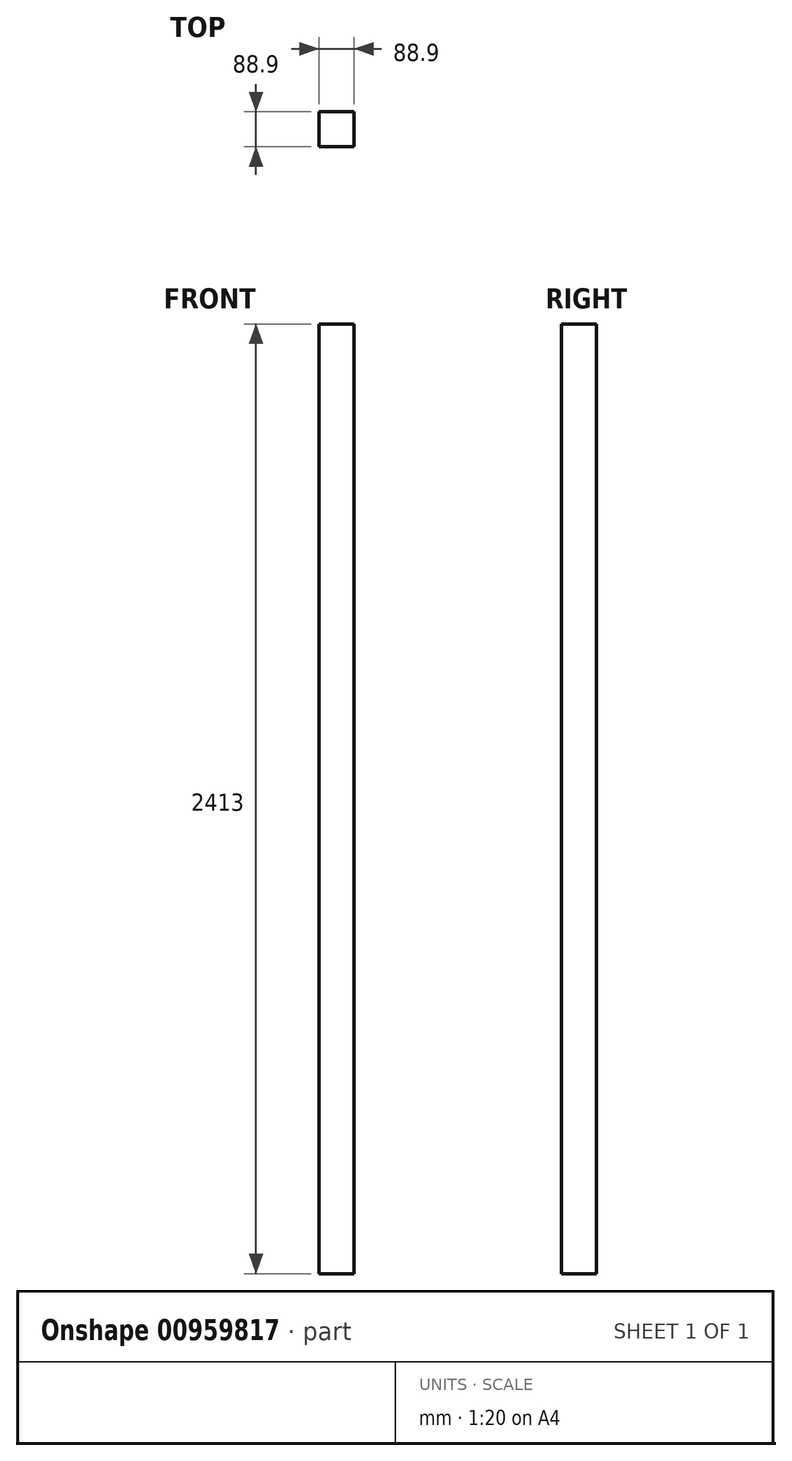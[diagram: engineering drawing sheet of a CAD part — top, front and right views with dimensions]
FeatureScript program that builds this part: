
annotation { "Feature Type Name" : "Feature", "Feature Type Description" : "" }
export const myFeature = defineFeature(function(context is Context, id is Id, definition is map)
    precondition{}
    {
        {
            var Q0;
            Q0=qCreatedBy(makeId("Top.planeOp"),FACE);
            var sketch = newSketch(context, id + "F0", { "sketchPlane" : qUnion([Q0])});
            skLineSegment(sketch, "E0.bottom", {"start": v(44.45, 44.45) * mm, "end": v(-44.45, 44.45) * mm});
            skLineSegment(sketch, "E0.top", {"start": v(44.45, -44.45) * mm, "end": v(-44.45, -44.45) * mm});
            skLineSegment(sketch, "E0.left", {"start": v(44.45, 44.45) * mm, "end": v(44.45, -44.45) * mm});
            skLineSegment(sketch, "E0.right", {"start": v(-44.45, 44.45) * mm, "end": v(-44.45, -44.45) * mm});
            skPoint(sketch, "E0.middle", {"position": v(0, 0) * mm});
            skSolve(sketch);
        }
        {
            var Q0;
            Q0=makeQuery(id+"F0.imprint","IMPRINT",FACE,{"disambiguationData":[TD([[makeQuery(id+"F0.imprint","IMPRINT",EDGE,{"derivedFrom":sQuery(id+"F0.wireOp",EDGE,"E0.bottom")}),1.0]])]});
            extrude(context, id + "F1", {"entities" : qUnion([Q0]), "depth" : 2413 * mm, "offsetDistance" : 25.4 * mm});
        }
    });
